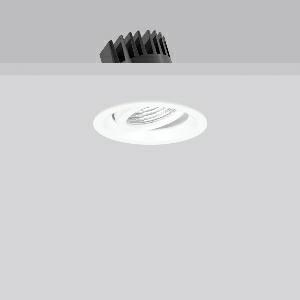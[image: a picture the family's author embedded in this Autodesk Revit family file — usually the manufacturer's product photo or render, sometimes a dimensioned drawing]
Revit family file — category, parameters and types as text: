
# Revit family: levido_swing_round_901835_002_2_76_1bf8
name_source: partatom
category: Lighting Fixtures
units: mm (PartAtom-declared; Revit-internal decimal feet)

## family parameters
Cut with Voids When Loaded = No
Host = Face
Light Source = No
Part Type = Normal
Room Calculation Point = No
Round Connector Dimension = Use Diameter
Shared = No

## types (1)
- MultiLumen 1 (1 x LED Modul 827, 650 lm, 2700)
    Apparent Load = 8 VA
    CIE Flux Codes = 91 96 99 100 100
    Color Rendering = 80
    Color Temperature = 2700
    Default Elevation = 1800 mm
    Description = Series: LEVIDO SWING round
Round recessed projector with very small dimensions. Die-cast aluminium cover, powder-coated. Extruded aluminium heat sink. Reflector: aluminium, highly polished anodised finish. With safety glass. Can be swivelled by ± 25°. Medium beam light distribution. Light beam 23°. MultiLumen: 2 steps adjustable luminous flux. Factory setting is the highest luminous flux. Suitable for Recessed ceiling mounting. Luminaire mounting with spring system. Including separate LED converter with connecting cable 250 mm. Suitable for through-wiring. Opal diffuser (PMMA) for uniform, homogenous light distribution available as an accessory. 
Colour: traffic white, matt (RAL 9016)
Diameter: 91 mm
Height: 2 mm
Cut-out diameter: 78 mm
Recess height: 80 mm
Luminaire: recess height: 80 mm
Lamp: LED
Socket: without socket
Colour temperature: 2700K
Colour rendering index (CRI): 80
System power: 7.5 W
Rated luminous flux: 650 lm
Luminous efficiency: 87 lm/W
System power 2: 12 W
Rated luminous flux 2: 1000 lm
Luminous efficiency 2: 83 lm/W
Control gear: Converter, dimmable, DALI
Protection class: II
Type of protection: IP 40
    Height = 0 mm  [stored 0 ft]
    Lamp = 1 x LED Modul 827
    Lamp Light Flux = 650 lm
    Lamp count = 1
    Length = 91 mm
    Lifetime = 50000 h
    Luminous efficacy = 87 lm/W
    Manufacturer = RZB
    ModVariant = No
    Model = 901835.002.2.76
    Mounting Place = Ceiling
    Mounting Type = Recessed
    Number of Poles = 1
    OnlyDefault = Yes
    Power Factor = 1
    Product Name = LEVIDO SWING round
    Product group = Recessed projectors
    ProductGroupID = 401
    Protection Class = Protection class II
    Protection Degree = IP 40
    RLX_Detail_Level = 1
    RLX_Emergency_Light_Flux = 0 lm
    RLX_Emergency_Type = 0
    RLX_Emergency_Type_DB = No
    RlxData = <blob elided: 61429 chars, md5=0f7d2b4f>
    Socket = socket
    Standby Power = 0 W
    System Light Flux = 650 lm
    System Power = 8 W
    Type Comments = MultiLumen 1
    Type Image = 901835.002.jpg
    URL = http://relux.com
    VarID = multilumen_1
    Voltage = 0 V
    Weight = 0.00 kg
    Width = 0 mm  [stored 0 ft]

note: [stored X ft] marks values corroborated as IEEE doubles in the binary element streams (Revit-internal decimal feet)

## geometry (parser evidence)
native form markers: Blend x4, Sweep x14
no freeform markers — native parametric forms only
